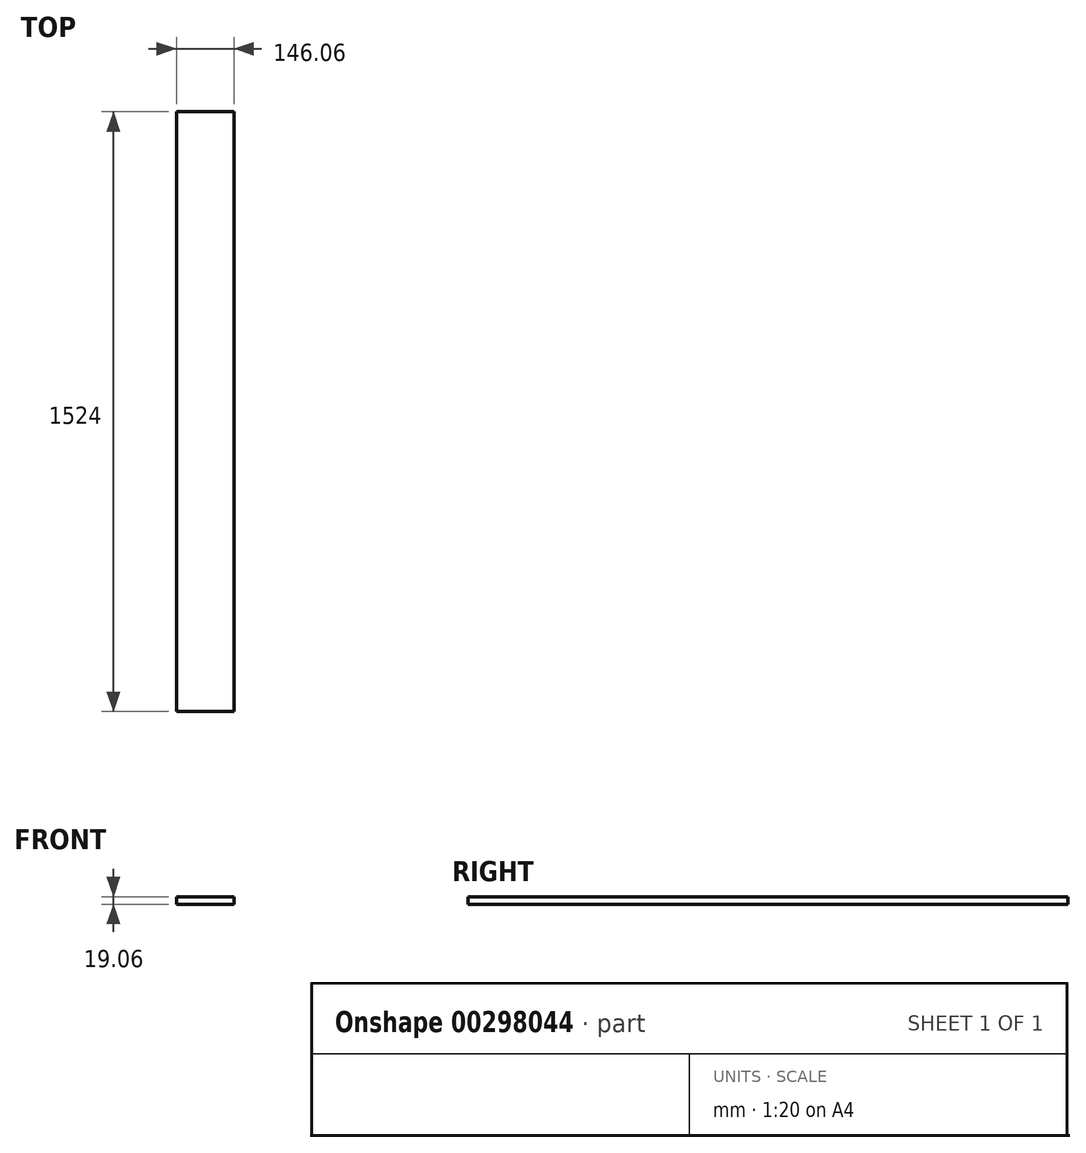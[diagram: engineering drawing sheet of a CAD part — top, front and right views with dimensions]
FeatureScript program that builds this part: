
annotation { "Feature Type Name" : "Feature", "Feature Type Description" : "" }
export const myFeature = defineFeature(function(context is Context, id is Id, definition is map)
    precondition{}
    {
        {
            var Q0;
            Q0=qCreatedBy(makeId("Front.planeOp"),FACE);
            var sketch = newSketch(context, id + "F0", { "sketchPlane" : qUnion([Q0])});
            skLineSegment(sketch, "E0.bottom", {"start": v(-73.03, -9.53) * mm, "end": v(73.03, -9.53) * mm});
            skLineSegment(sketch, "E0.top", {"start": v(-73.03, 9.52) * mm, "end": v(73.03, 9.52) * mm});
            skLineSegment(sketch, "E0.left", {"start": v(-73.03, -9.53) * mm, "end": v(-73.03, 9.53) * mm});
            skLineSegment(sketch, "E0.right", {"start": v(73.03, -9.53) * mm, "end": v(73.03, 9.53) * mm});
            skPoint(sketch, "E0.middle", {"position": v(0, 0) * mm});
            skLineSegment(sketch, "E1.bottom", {"start": v(-73.03, 3.18) * mm, "end": v(-66.68, 3.18) * mm});
            skLineSegment(sketch, "E1.top", {"start": v(-73.03, -3.17) * mm, "end": v(-66.68, -3.17) * mm});
            skLineSegment(sketch, "E1.left", {"start": v(-73.03, 3.18) * mm, "end": v(-73.03, -3.17) * mm});
            skLineSegment(sketch, "E1.right", {"start": v(-66.68, 3.18) * mm, "end": v(-66.68, -3.17) * mm});
            skPoint(sketch, "E1.middle", {"position": v(-69.85, 0) * mm});
            skLineSegment(sketch, "E2.bottom", {"start": v(73.03, 3.18) * mm, "end": v(66.67, 3.18) * mm});
            skLineSegment(sketch, "E2.top", {"start": v(73.02, -3.17) * mm, "end": v(66.67, -3.17) * mm});
            skLineSegment(sketch, "E2.left", {"start": v(73.03, 3.18) * mm, "end": v(73.03, -3.17) * mm});
            skLineSegment(sketch, "E2.right", {"start": v(66.67, 3.18) * mm, "end": v(66.67, -3.17) * mm});
            skPoint(sketch, "E2.middle", {"position": v(69.85, 0) * mm});
            skSolve(sketch);
        }
        {
            var Q0;
            {var subQ6=sQuery(id+"F0.wireOp",EDGE,"E0.bottom");Q0=makeQuery(id+"F0.imprint","IMPRINT",FACE,{"disambiguationData":[TD([[makeQuery(id+"F0.imprint","IMPRINT",EDGE,{"derivedFrom":subQ6}),1.0]])]});}
            var Q1;
            Q1=makeQuery(id+"F0.imprint","IMPRINT",FACE,{"disambiguationData":[TD([[makeQuery(id+"F0.imprint","IMPRINT",EDGE,{"derivedFrom":sQuery(id+"F0.wireOp",EDGE,"E1.bottom")}),-1.0]])]});
            var Q2;
            Q2=makeQuery(id+"F0.imprint","IMPRINT",FACE,{"disambiguationData":[TD([[makeQuery(id+"F0.imprint","IMPRINT",EDGE,{"derivedFrom":sQuery(id+"F0.wireOp",EDGE,"E2.bottom")}),1.0]])]});
            extrude(context, id + "F1", {"entities" : qUnion([Q0, Q1, Q2]), "endBound" : BoundingType.SYMMETRIC, "depth" : 1524 * mm});
        }
    });
